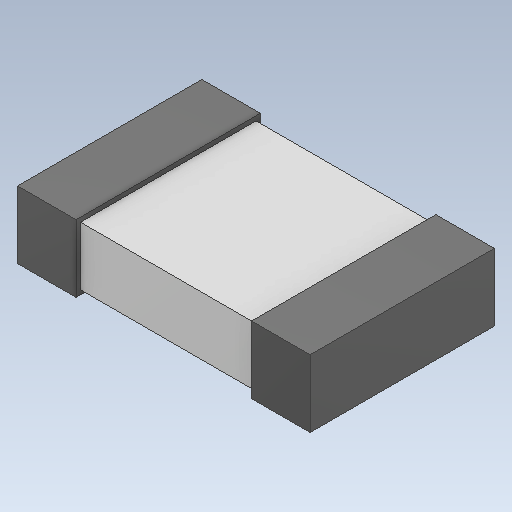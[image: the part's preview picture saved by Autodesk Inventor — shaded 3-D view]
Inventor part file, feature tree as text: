
AUTODESK INVENTOR PART (.ipt)
format: ipt  version: 2020 (Build 240168000, 168)  size: 98,304 bytes
history: native  units: mm
features: other x1, extrude x1
ambient origin geometry x8: Origin, YZ Plane, XZ Plane, XY Plane, X Axis, Y Axis, Z Axis, Center Point
bodies: Body1 (feature_tree)
feature tree (2):
  other  "Твердое тело1"
  extrude  "Extrude2"  [1 undecoded]
note: 1 required parameter value undecoded (feature->parameter linkage not recoverable at this tier; creation-order binding heuristic only, values carry confidence <= 0.55)
